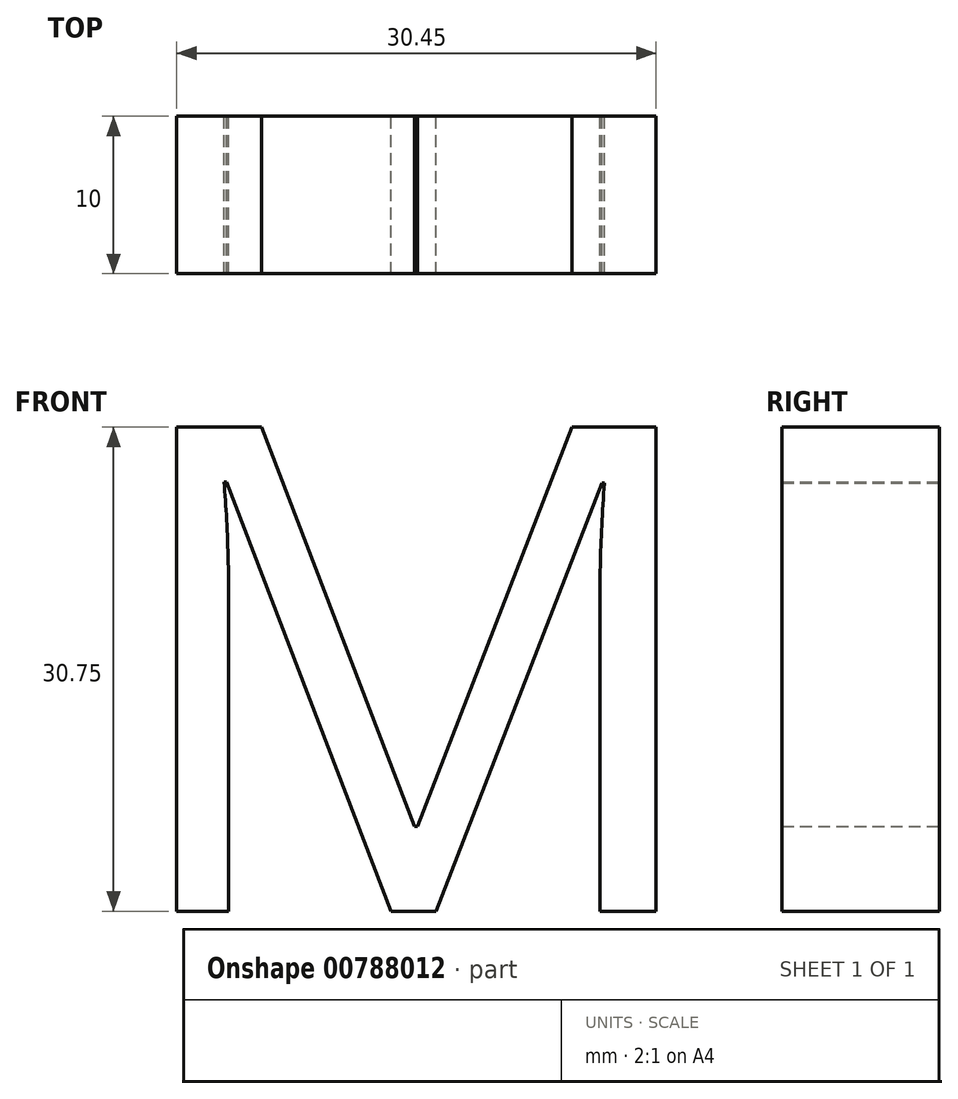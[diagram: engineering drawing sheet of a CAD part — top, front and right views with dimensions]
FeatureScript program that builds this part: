
annotation { "Feature Type Name" : "Feature", "Feature Type Description" : "" }
export const myFeature = defineFeature(function(context is Context, id is Id, definition is map)
    precondition{}
    {
        {
            var Q0;
            Q0=qCreatedBy(makeId("Front.planeOp"),FACE);
            var sketch = newSketch(context, id + "F0", { "sketchPlane" : qUnion([Q0])});
            skText(sketch, "E0", { "text": "M", "fontName": "OpenSans-Regular.ttf"});
            const initialGuessF0  = {"E0": [-0.03747, 0, 1, 0, 0.03101]};
            skSetInitialGuess(sketch, initialGuessF0);
            skSolve(sketch);
        }
        {
            var Q0;
            Q0 = qSketchRegion(id + "F0", true);
            extrude(context, id + "F1", {"entities" : qUnion([Q0]), "depth" : 10 * mm, "offsetDistance" : 25.4 * mm});
        }
    });
